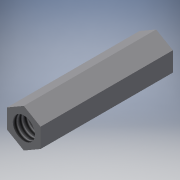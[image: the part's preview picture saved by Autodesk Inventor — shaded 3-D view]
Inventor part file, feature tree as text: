
AUTODESK INVENTOR PART (.ipt)
format: ipt  version: 2018.1 (Build 221171000, 171)  size: 109,568 bytes
history: native  units: mm
features: hole x5, sketch x4, extrude x1
ambient origin geometry x8: Origin, YZ Plane, XZ Plane, XY Plane, X Axis, Y Axis, Z Axis, Center Point
bodies: Solid1 (feature_tree)
feature tree (10):
  extrude  "Extrusion1"  Depth=12.0mm TaperAngle=0.0deg
  hole  "Hole1"  [1 undecoded]
  hole  "Hole3"  [1 undecoded]
  hole  "Hole5"  [1 undecoded]
  sketch  "Sketch1"  dims[d0=1.75mm d1=12.0mm d2=0.0mm]
  sketch  "Sketch2"  dims[d3=2.013mm d4=12.0mm d5=4.0mm d6=2.0mm d7=90.0deg d8=7.6mm d9=20.594885mm]
  sketch  "Sketch3"  dims[d10=2.013mm d11=4.52mm d12=4.0mm d13=2.0mm d14=90.0deg d15=5.77mm d16=120.0deg]
  hole  "Hole2"  [1 undecoded]
  sketch  "Sketch4"  dims[d17=2.013mm d18=6.202mm d19=4.0mm d20=2.0mm d21=90.0deg d22=7.452mm d23=120.0deg]
  hole  "Hole4"  [1 undecoded]
note: 5 required parameter values undecoded (feature->parameter linkage not recoverable at this tier; creation-order binding heuristic only, values carry confidence <= 0.55)
